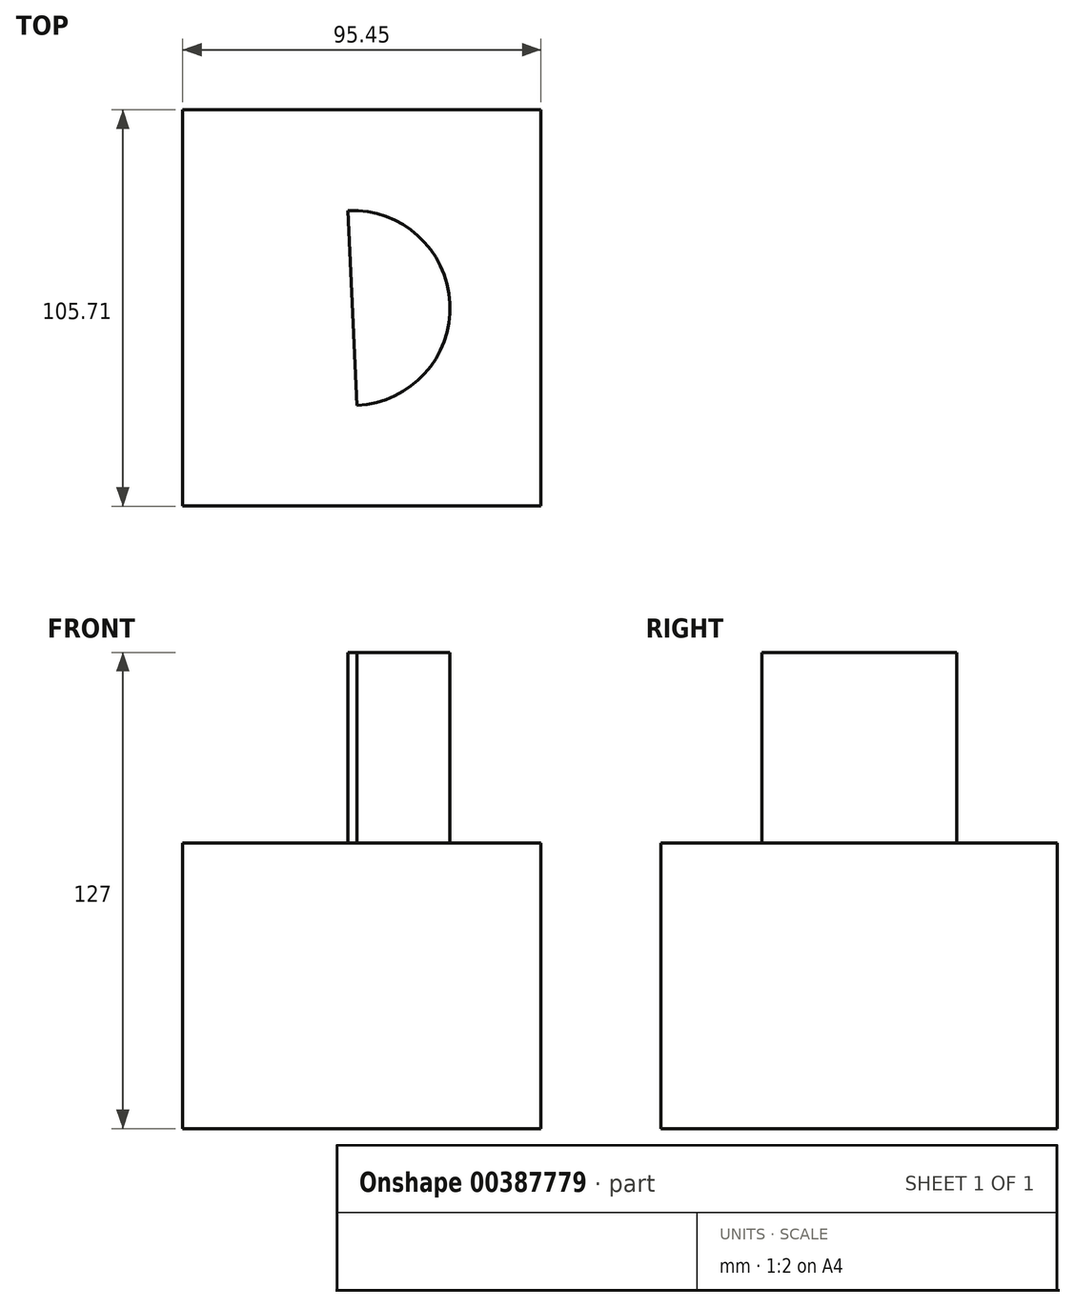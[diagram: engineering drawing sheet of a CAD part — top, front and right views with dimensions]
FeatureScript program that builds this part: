
annotation { "Feature Type Name" : "Feature", "Feature Type Description" : "" }
export const myFeature = defineFeature(function(context is Context, id is Id, definition is map)
    precondition{}
    {
        {
            var Q0;
            Q0=qCreatedBy(makeId("Top.planeOp"),FACE);
            var sketch = newSketch(context, id + "F0", { "sketchPlane" : qUnion([Q0])});
            skLineSegment(sketch, "E0.bottom", {"start": v(-75.58, -74.72) * mm, "end": v(19.87, -74.72) * mm});
            skLineSegment(sketch, "E0.top", {"start": v(-75.58, 30.99) * mm, "end": v(19.87, 30.99) * mm});
            skLineSegment(sketch, "E0.left", {"start": v(-75.58, -74.72) * mm, "end": v(-75.58, 30.99) * mm});
            skLineSegment(sketch, "E0.right", {"start": v(19.87, -74.72) * mm, "end": v(19.87, 30.99) * mm});
            skSolve(sketch);
        }
        {
            var Q0;
            Q0=makeQuery(id+"F0.imprint","IMPRINT",FACE,{"disambiguationData":[TD([[makeQuery(id+"F0.imprint","IMPRINT",EDGE,{"derivedFrom":sQuery(id+"F0.wireOp",EDGE,"E0.bottom")}),1.0]])]});
            extrude(context, id + "F1", {"entities" : qUnion([Q0]), "depth" : 76.2 * mm});
        }
        {
            var Q0;
            Q0=makeQuery(id+"F1.opExtrude","CAP_FACE",FACE,{"disambiguationData":[OSD([sQuery(id+"F0.wireOp",EDGE,"E0.bottom"),sQuery(id+"F0.wireOp",EDGE,"E0.top"),sQuery(id+"F0.wireOp",EDGE,"E0.left"),sQuery(id+"F0.wireOp",EDGE,"E0.right")])],"isStart":false});
            var sketch = newSketch(context, id + "F2", { "sketchPlane" : qUnion([Q0])});
            skLineSegment(sketch, "E1", {"start": v(-27.85, -69.23) * mm, "end": v(-23.88, -53.83) * mm});
            skPoint(sketch, "E1.startSnap0", {"position": v(-27.85, -74.72) * mm});
            skLineSegment(sketch, "E2", {"start": v(-32.83, 30.99) * mm, "end": v(-27.85, -74.72) * mm});
            skCircle(sketch, "E3", {"center": v(-30.34, -21.86) * mm, "radius": 26 * mm});
            skSolve(sketch);
        }
        {
            var Q0;
            {var subQ0=sQuery(id+"F2.wireOp",EDGE,"E3");var subQ1=sQuery(id+"F2.wireOp",EDGE,"E2");var subQ2=makeQuery(id+"F2.imprint","INTERSECT",VERTEX,{"disambiguationData":[OD(0.0)],"derivedFrom":[subQ1,subQ0]});Q0=makeQuery(id+"F2.imprint","IMPRINT",FACE,{"disambiguationData":[TD([[makeQuery(id+"F2.imprint","IMPRINT",EDGE,{"disambiguationData":[TD([[subQ2,-1.0]])],"derivedFrom":subQ1}),1.0]])]});}
            extrude(context, id + "F3", {"entities" : qUnion([Q0]), "operationType" : NewBodyOperationType.ADD, "depth" : 50.8 * mm});
        }
    });
